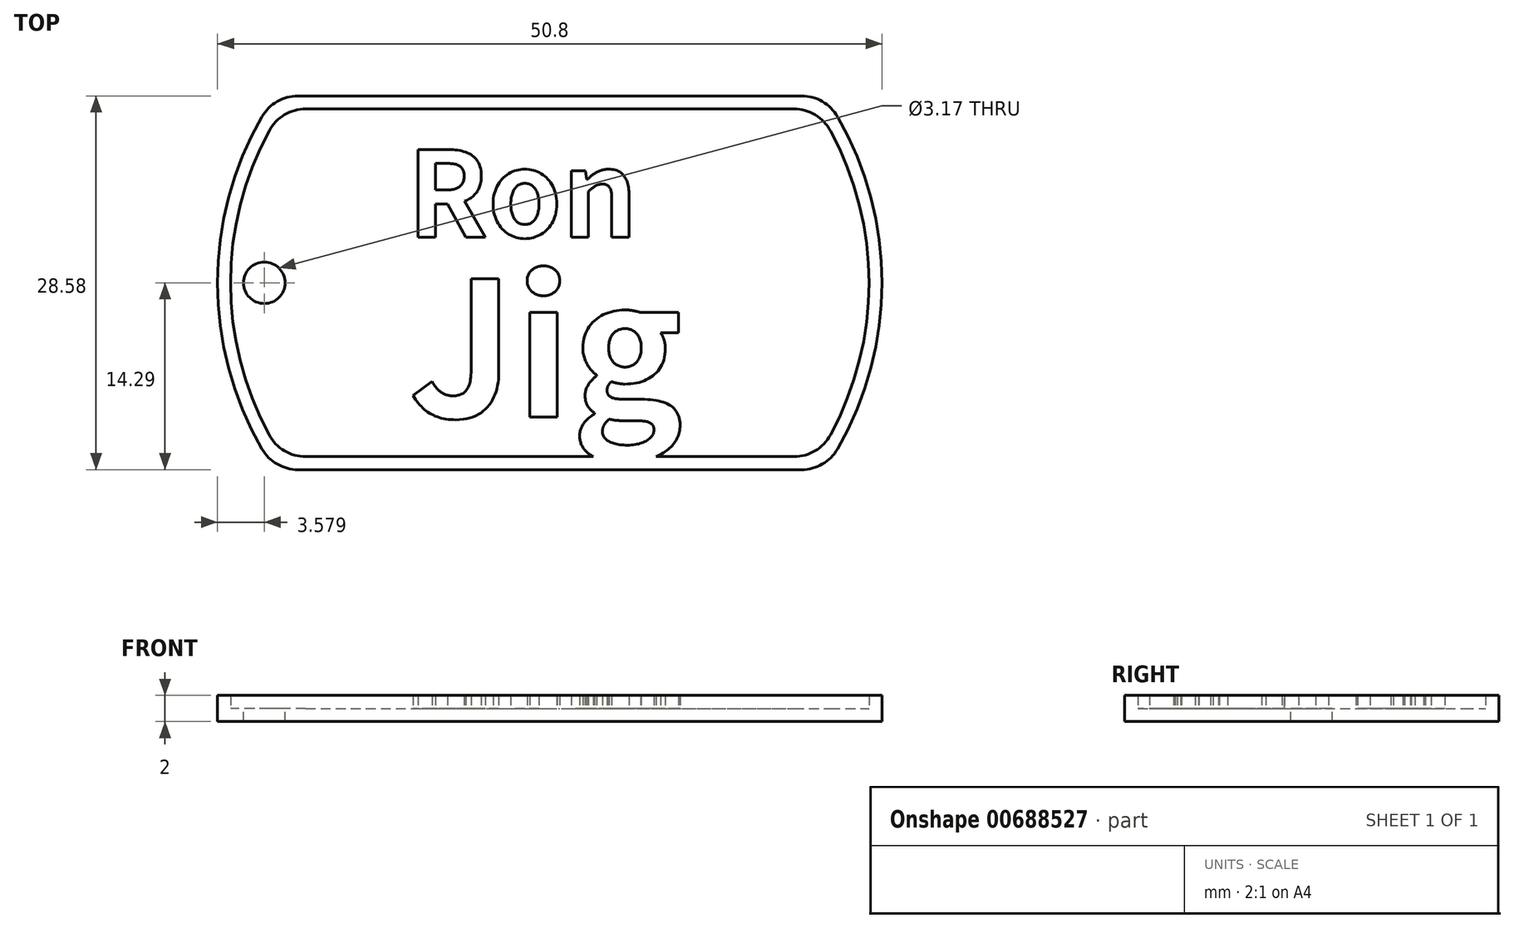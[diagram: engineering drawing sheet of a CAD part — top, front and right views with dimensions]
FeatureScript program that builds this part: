
annotation { "Feature Type Name" : "Feature", "Feature Type Description" : "" }
export const myFeature = defineFeature(function(context is Context, id is Id, definition is map)
    precondition{}
    {
        {
            var Q0;
            Q0=qCreatedBy(makeId("Top.planeOp"),FACE);
            var sketch = newSketch(context, id + "F0", { "sketchPlane" : qUnion([Q0])});
            skArc(sketch, "E0", {"start": v(-22, 12.7) * mm, "mid": v(-25.4, 0) * mm, "end": v(-22, -12.7) * mm});
            skLineSegment(sketch, "E1.top", {"start": v(-19.25, -14.29) * mm, "end": v(19.25, -14.29) * mm});
            skArc(sketch, "E2.trimOffspring", {"start": v(22, -12.7) * mm, "mid": v(25.4, 0) * mm, "end": v(22, 12.7) * mm});
            skLineSegment(sketch, "E3", {"start": v(-19.25, 14.29) * mm, "end": v(19.25, 14.29) * mm});
            skPoint(sketch, "E4.visualSharp", {"position": v(-21, 14.29) * mm});
            skArc(sketch, "E4.filletArc", {"start": v(-19.25, 14.29) * mm, "mid": v(-20.83, 13.86) * mm, "end": v(-22, 12.7) * mm});
            skPoint(sketch, "E5.visualSharp", {"position": v(21, 14.29) * mm});
            skArc(sketch, "E5.filletArc", {"start": v(22, 12.7) * mm, "mid": v(20.83, 13.86) * mm, "end": v(19.25, 14.29) * mm});
            skPoint(sketch, "E6.visualSharp", {"position": v(21, -14.29) * mm});
            skArc(sketch, "E6.filletArc", {"start": v(19.25, -14.29) * mm, "mid": v(20.83, -13.86) * mm, "end": v(22, -12.7) * mm});
            skPoint(sketch, "E7.visualSharp", {"position": v(-21, -14.29) * mm});
            skArc(sketch, "E7.filletArc", {"start": v(-22, -12.7) * mm, "mid": v(-20.83, -13.86) * mm, "end": v(-19.25, -14.29) * mm});
            skSolve(sketch);
        }
        {
            var Q0;
            Q0=makeQuery(id+"F0.imprint","IMPRINT",FACE,{"disambiguationData":[TD([[makeQuery(id+"F0.imprint","IMPRINT",EDGE,{"derivedFrom":sQuery(id+"F0.wireOp",EDGE,"E0")}),1.0]])]});
            extrude(context, id + "F1", {"entities" : qUnion([Q0]), "depth" : 1 * mm, "offsetDistance" : 25.4 * mm});
        }
        {
            var Q0;
            Q0=makeQuery(id+"F1.opExtrude","CAP_FACE",FACE,{"disambiguationData":[OSD([sQuery(id+"F0.wireOp",EDGE,"E0"),sQuery(id+"F0.wireOp",EDGE,"E1.top"),sQuery(id+"F0.wireOp",EDGE,"E2.trimOffspring"),sQuery(id+"F0.wireOp",EDGE,"E3"),sQuery(id+"F0.wireOp",EDGE,"E4.filletArc"),sQuery(id+"F0.wireOp",EDGE,"E5.filletArc"),sQuery(id+"F0.wireOp",EDGE,"E6.filletArc"),sQuery(id+"F0.wireOp",EDGE,"E7.filletArc")])],"isStart":false});
            var sketch = newSketch(context, id + "F2", { "sketchPlane" : qUnion([Q0])});
            skLineSegment(sketch, "E8.0", {"start": v(-18.66, 13.29) * mm, "end": v(18.66, 13.29) * mm});
            skArc(sketch, "E8.1", {"start": v(-21.45, 11.63) * mm, "mid": v(-24.4, 0) * mm, "end": v(-21.45, -11.63) * mm});
            skLineSegment(sketch, "E8.2", {"start": v(-18.66, -13.29) * mm, "end": v(18.66, -13.29) * mm});
            skArc(sketch, "E8.3", {"start": v(21.45, -11.63) * mm, "mid": v(24.4, 0) * mm, "end": v(21.45, 11.63) * mm});
            skPoint(sketch, "E9.visualSharp", {"position": v(-20.46, 13.29) * mm});
            skArc(sketch, "E9.filletArc", {"start": v(-18.66, 13.29) * mm, "mid": v(-20.29, 12.84) * mm, "end": v(-21.45, 11.63) * mm});
            skPoint(sketch, "E10.visualSharp", {"position": v(20.46, 13.29) * mm});
            skArc(sketch, "E10.filletArc", {"start": v(21.45, 11.63) * mm, "mid": v(20.29, 12.84) * mm, "end": v(18.66, 13.29) * mm});
            skPoint(sketch, "E11.visualSharp", {"position": v(20.46, -13.29) * mm});
            skArc(sketch, "E11.filletArc", {"start": v(18.66, -13.29) * mm, "mid": v(20.29, -12.84) * mm, "end": v(21.45, -11.63) * mm});
            skPoint(sketch, "E12.visualSharp", {"position": v(-20.46, -13.29) * mm});
            skArc(sketch, "E12.filletArc", {"start": v(-21.45, -11.63) * mm, "mid": v(-20.29, -12.84) * mm, "end": v(-18.66, -13.29) * mm});
            skLineSegment(sketch, "E13.0", {"start": v(-19.25, 14.29) * mm, "end": v(19.25, 14.29) * mm});
            skArc(sketch, "E13.1", {"start": v(-22, 12.7) * mm, "mid": v(-25.4, 0) * mm, "end": v(-22, -12.7) * mm});
            skLineSegment(sketch, "E13.2", {"start": v(-19.25, -14.29) * mm, "end": v(19.25, -14.29) * mm});
            skArc(sketch, "E13.3", {"start": v(22, -12.7) * mm, "mid": v(25.4, 0) * mm, "end": v(22, 12.7) * mm});
            skPoint(sketch, "E14.visualSharp", {"position": v(-21, -14.29) * mm});
            skArc(sketch, "E14.filletArc", {"start": v(-22, -12.7) * mm, "mid": v(-20.83, -13.86) * mm, "end": v(-19.25, -14.29) * mm});
            skPoint(sketch, "E15.visualSharp", {"position": v(21, -14.29) * mm});
            skArc(sketch, "E15.filletArc", {"start": v(19.25, -14.29) * mm, "mid": v(20.83, -13.86) * mm, "end": v(22, -12.7) * mm});
            skPoint(sketch, "E16.visualSharp", {"position": v(21, 14.29) * mm});
            skArc(sketch, "E16.filletArc", {"start": v(22, 12.7) * mm, "mid": v(20.83, 13.86) * mm, "end": v(19.25, 14.29) * mm});
            skPoint(sketch, "E17.visualSharp", {"position": v(-21, 14.29) * mm});
            skArc(sketch, "E17.filletArc", {"start": v(-19.25, 14.29) * mm, "mid": v(-20.83, 13.86) * mm, "end": v(-22, 12.7) * mm});
            skSolve(sketch);
        }
        {
            var Q0;
            Q0=makeQuery(id+"F2.imprint","IMPRINT",FACE,{"disambiguationData":[TD([[makeQuery(id+"F2.imprint","IMPRINT",EDGE,{"derivedFrom":sQuery(id+"F2.wireOp",EDGE,"E8.0")}),1.0]])]});
            extrude(context, id + "F3", {"entities" : qUnion([Q0]), "operationType" : NewBodyOperationType.ADD, "depth" : 1 * mm, "offsetDistance" : 25.4 * mm});
        }
        {
            var Q0;
            Q0=makeQuery(id+"F1.opExtrude","CAP_FACE",FACE,{"disambiguationData":[OSD([sQuery(id+"F0.wireOp",EDGE,"E0"),sQuery(id+"F0.wireOp",EDGE,"E1.top"),sQuery(id+"F0.wireOp",EDGE,"E2.trimOffspring"),sQuery(id+"F0.wireOp",EDGE,"E3"),sQuery(id+"F0.wireOp",EDGE,"E4.filletArc"),sQuery(id+"F0.wireOp",EDGE,"E5.filletArc"),sQuery(id+"F0.wireOp",EDGE,"E6.filletArc"),sQuery(id+"F0.wireOp",EDGE,"E7.filletArc")])],"isStart":false});
            var sketch = newSketch(context, id + "F4", { "sketchPlane" : qUnion([Q0])});
            skCircle(sketch, "E18", {"center": v(-21.82, 0) * mm, "radius": 1.59 * mm});
            skSolve(sketch);
        }
        {
            var Q0;
            Q0=makeQuery(id+"F4.imprint","IMPRINT",FACE,{"disambiguationData":[TD([[makeQuery(id+"F4.imprint","IMPRINT",EDGE,{"derivedFrom":sQuery(id+"F4.wireOp",EDGE,"E18")}),1.0]])]});
            extrude(context, id + "F5", {"entities" : qUnion([Q0]), "operationType" : NewBodyOperationType.REMOVE, "oppositeDirection" : true, "depth" : 1 * mm, "offsetDistance" : 25.4 * mm});
        }
        {
            var Q0;
            Q0=makeQuery(id+"F1.opExtrude","CAP_FACE",FACE,{"disambiguationData":[OSD([sQuery(id+"F0.wireOp",EDGE,"E0"),sQuery(id+"F0.wireOp",EDGE,"E1.top"),sQuery(id+"F0.wireOp",EDGE,"E2.trimOffspring"),sQuery(id+"F0.wireOp",EDGE,"E3"),sQuery(id+"F0.wireOp",EDGE,"E4.filletArc"),sQuery(id+"F0.wireOp",EDGE,"E5.filletArc"),sQuery(id+"F0.wireOp",EDGE,"E6.filletArc"),sQuery(id+"F0.wireOp",EDGE,"E7.filletArc")])],"isStart":false});
            var sketch = newSketch(context, id + "F6", { "sketchPlane" : qUnion([Q0])});
            skText(sketch, "E19", { "text": "Ron", "fontName": "NotoSansCJKkr-Bold.otf"});
            const initialGuessF6  = {"E19": [-0.0109, 0.0035, 1, 0, 0.00651]};
            skSetInitialGuess(sketch, initialGuessF6);
            skSolve(sketch);
        }
        {
            var Q0;
            Q0 = qSketchRegion(id + "F6", true);
            extrude(context, id + "F7", {"entities" : qUnion([Q0]), "operationType" : NewBodyOperationType.ADD, "depth" : 1 * mm, "offsetDistance" : 25.4 * mm});
        }
        {
            var Q0;
            Q0=makeQuery(id+"F7.boolean.opBoolean","SPLIT",FACE,{"disambiguationData":[TD([makeQuery(id+"F3.opExtrude","SWEPT_FACE",FACE,{"disambiguationData":[OSD([sQuery(id+"F2.wireOp",EDGE,"E8.0")])]})])],"derivedFrom":makeQuery(id+"F1.opExtrude","CAP_FACE",FACE,{"disambiguationData":[OSD([sQuery(id+"F0.wireOp",EDGE,"E0"),sQuery(id+"F0.wireOp",EDGE,"E1.top"),sQuery(id+"F0.wireOp",EDGE,"E2.trimOffspring"),sQuery(id+"F0.wireOp",EDGE,"E3"),sQuery(id+"F0.wireOp",EDGE,"E4.filletArc"),sQuery(id+"F0.wireOp",EDGE,"E5.filletArc"),sQuery(id+"F0.wireOp",EDGE,"E6.filletArc"),sQuery(id+"F0.wireOp",EDGE,"E7.filletArc")])],"isStart":false})});
            var sketch = newSketch(context, id + "F8", { "sketchPlane" : qUnion([Q0])});
            skText(sketch, "E20", { "text": "Jig", "fontName": "NotoSansCJKjp-Bold.otf"});
            const initialGuessF8  = {"E20": [-0.01077, -0.01027, 1, 0, 0.01028]};
            skSetInitialGuess(sketch, initialGuessF8);
            skSolve(sketch);
        }
        {
            var Q0;
            Q0 = qSketchRegion(id + "F8", true);
            extrude(context, id + "F9", {"entities" : qUnion([Q0]), "operationType" : NewBodyOperationType.ADD, "depth" : 1 * mm, "offsetDistance" : 25.4 * mm});
        }
    });
